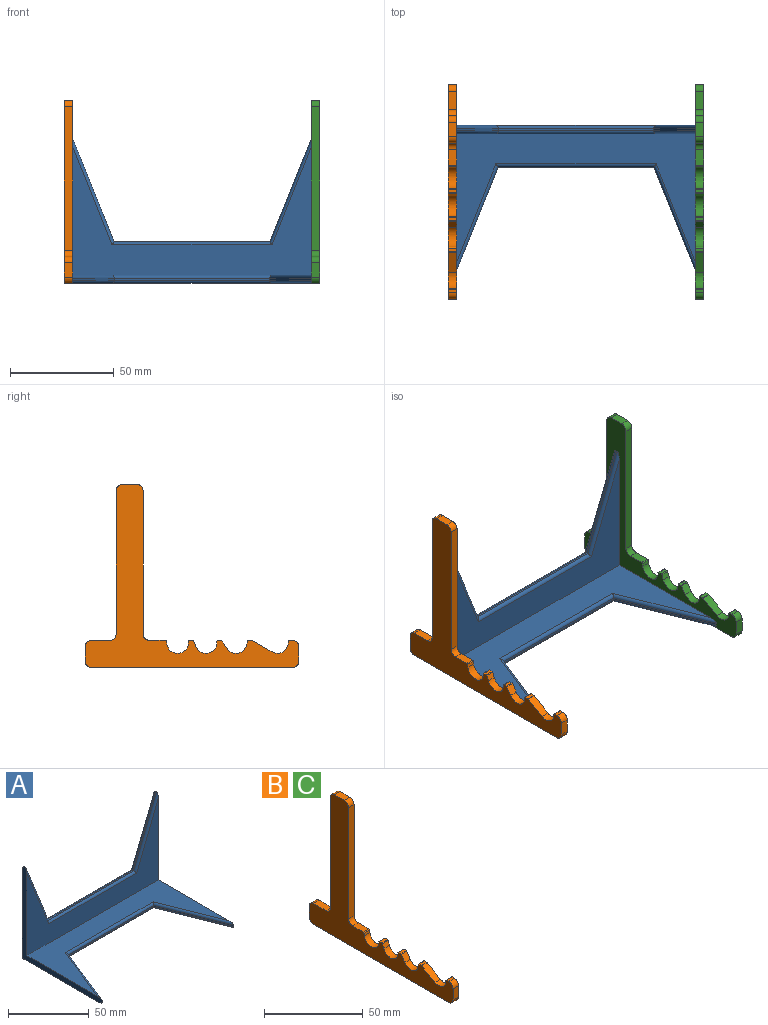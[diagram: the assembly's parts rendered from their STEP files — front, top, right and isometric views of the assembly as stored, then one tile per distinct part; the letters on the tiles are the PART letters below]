
ASSEMBLY  parts=3 mates=2
PART A: 25 faces, bbox 117.8x70x70 mm
  f0: plane 115x61.96mm, normal (0,-1,0), area 2568.5mm2, adj f5,f6,f7,f15,f16,f17
  f1: plane 115x64.46mm, normal (0,1,0), area 2856mm2, adj f6,f7,f12,f13,f14,f24
  f2: plane 75x1mm, normal (0,0,1), area 75mm2, adj f10,f11,f13,f16
  f3: plane 75x1mm, normal (0,-1,0), area 75mm2, adj f8,f9,f19,f22
  f4: plane 115x64.46mm, normal (0,0,-1), area 2856mm2, adj f6,f7,f18,f19,f20,f24
  f5: plane 115x61.96mm, normal (0,0,1), area 2568.5mm2, adj f0,f6,f7,f21,f22,f23
  f6: plane 70x70mm, normal (1,0,0), area 538.3mm2, adj f0,f1,f4,f5,f9,f10,f12,f17
  f7: plane 70x70mm, normal (-1,0,0), area 538.3mm2, adj f0,f1,f4,f5,f8,f11,f14,f15
  f8: plane 50x20mm, normal (0.93,-0.37,0), area 53.9mm2, adj f3,f7,f18,f23
  f9: plane 50x20mm, normal (-0.93,-0.37,0), area 53.9mm2, adj f3,f6,f20,f21
  f10: plane 50x20mm, normal (-0.93,0,0.37), area 53.9mm2, adj f2,f6,f12,f17
  f11: plane 50x20mm, normal (0.93,0,0.37), area 53.9mm2, adj f2,f7,f14,f15
  f12: cylinder r=1.5mm len=51.5mm, axis (0.37,0,0.93), area 124.5mm2, adj f1,f6,f10,f13
  f13: cylinder r=1.5mm len=77.03mm, axis (-1,0,0), area 178.5mm2, adj f1,f2,f12,f14
  f14: cylinder r=1.5mm len=51.5mm, axis (0.37,0,-0.93), area 124.5mm2, adj f1,f7,f11,f13
  f15: cylinder r=1.5mm len=51.5mm, axis (-0.37,0,0.93), area 124.5mm2, adj f0,f7,f11,f16
  f16: cylinder r=1.5mm len=77.03mm, axis (-1,0,0), area 178.5mm2, adj f0,f2,f15,f17
  f17: cylinder r=1.5mm len=51.5mm, axis (-0.37,0,-0.93), area 124.5mm2, adj f0,f6,f10,f16
  f18: cylinder r=1.5mm len=51.5mm, axis (-0.37,-0.93,0), area 124.5mm2, adj f4,f7,f8,f19
  f19: cylinder r=1.5mm len=77.03mm, axis (-1,0,0), area 178.5mm2, adj f3,f4,f18,f20
  f20: cylinder r=1.5mm len=51.5mm, axis (-0.37,0.93,0), area 124.5mm2, adj f4,f6,f9,f19
  f21: cylinder r=1.5mm len=51.5mm, axis (0.37,-0.93,0), area 124.5mm2, adj f5,f6,f9,f22
  f22: cylinder r=1.5mm len=77.03mm, axis (-1,0,0), area 178.5mm2, adj f3,f5,f21,f23
  f23: cylinder r=1.5mm len=51.5mm, axis (0.37,0.93,0), area 124.5mm2, adj f5,f7,f8,f22
  f24: cylinder r=1.5mm len=115mm, axis (-1,0,0), area 271mm2, adj f1,f4,f6,f7
PART B: 38 faces, bbox 4x103x88 mm
  f0: plane 4x1.6mm, normal (0,0,1), area 6.4mm2, adj f1,f3,f31,f32
  f1: plane 103x88mm, normal (1,0,0), area 2071.5mm2, adj f0,f2,f4,f5,f6,f7,f8,f9
  f2: plane 4x1.48mm, normal (0,0,1), area 5.9mm2, adj f1,f3,f33,f34
  f3: plane 103x88mm, normal (-1,0,0), area 2071.5mm2, adj f0,f2,f4,f5,f6,f7,f8,f9
  f4: plane 4x1.72mm, normal (0,0,1), area 6.9mm2, adj f1,f3,f35,f36
  f5: plane 4x1.63mm, normal (0,0,1), area 6.5mm2, adj f1,f3,f23,f37
  f6: plane 69x4mm, normal (0,-1,0), area 276mm2, adj f1,f3,f22,f29
  f7: plane 7.67x4mm, normal (0,0,1), area 30.7mm2, adj f1,f3,f22,f30
  f8: plane 7x4mm, normal (0,-1,0), area 28mm2, adj f1,f3,f23,f24
  f9: plane 97x4mm, normal (0,0,-1), area 388mm2, adj f1,f3,f24,f25
  f10: plane 7x4mm, normal (0,1,0), area 28mm2, adj f1,f3,f25,f26
  f11: plane 9x4mm, normal (0,0,1), area 36mm2, adj f1,f3,f26,f27
  f12: plane 69x4mm, normal (0,1,0), area 276mm2, adj f1,f3,f27,f28
  f13: plane 7x4mm, normal (0,0,1), area 28mm2, adj f1,f3,f28,f29
  f14: cylinder r=5.25mm len=7.86mm, axis (1,0,0), area 45.7mm2, adj f1,f3,f15,f37
  f15: plane 9.58x5.49mm, normal (0,-0.5,0.87), area 44.2mm2, adj f1,f3,f14,f36
  f16: plane 4x3.75mm, normal (0,-0.82,0.57), area 18.2mm2, adj f1,f3,f17,f34
  f17: cylinder r=5.25mm len=9.58mm, axis (1,0,0), area 55.2mm2, adj f1,f3,f16,f35
  f18: plane 4x2.54mm, normal (0,-0.94,0.35), area 10.9mm2, adj f1,f3,f19,f32
  f19: cylinder r=5.25mm len=10.16mm, axis (1,0,0), area 60.2mm2, adj f1,f3,f18,f33
  f20: plane 4x1.42mm, normal (0,-0.99,0.16), area 5.7mm2, adj f1,f3,f21,f30
  f21: cylinder r=5.25mm len=10.43mm, axis (1,0,0), area 64.4mm2, adj f1,f3,f20,f31
  f22: cylinder r=3mm len=4mm, axis (-1,0,0), area 18.8mm2, adj f1,f3,f6,f7
  f23: cylinder r=3mm len=4mm, axis (-1,0,0), area 18.8mm2, adj f1,f3,f5,f8
  f24: cylinder r=3mm len=4mm, axis (-1,0,0), area 18.8mm2, adj f1,f3,f8,f9
  f25: cylinder r=3mm len=4mm, axis (-1,0,0), area 18.8mm2, adj f1,f3,f9,f10
  f26: cylinder r=3mm len=4mm, axis (1,0,0), area 18.8mm2, adj f1,f3,f10,f11
  f27: cylinder r=3mm len=4mm, axis (1,0,0), area 18.8mm2, adj f1,f3,f11,f12
  f28: cylinder r=3mm len=4mm, axis (-1,0,0), area 18.8mm2, adj f1,f3,f12,f13
  f29: cylinder r=3mm len=4mm, axis (-1,0,0), area 18.8mm2, adj f1,f3,f6,f13
  f30: cylinder r=0.5mm len=4mm, axis (1,0,0), area 2.8mm2, adj f1,f3,f7,f20
  f31: cylinder r=0.5mm len=4mm, axis (1,0,0), area 3.3mm2, adj f0,f1,f3,f21
  f32: cylinder r=0.5mm len=4mm, axis (1,0,0), area 2.4mm2, adj f0,f1,f3,f18
  f33: cylinder r=0.5mm len=4mm, axis (1,0,0), area 3.3mm2, adj f1,f2,f3,f19
  f34: cylinder r=0.5mm len=4mm, axis (1,0,0), area 1.9mm2, adj f1,f2,f3,f16
  f35: cylinder r=0.5mm len=4mm, axis (1,0,0), area 3.3mm2, adj f1,f3,f4,f17
  f36: cylinder r=0.5mm len=4mm, axis (1,0,0), area 1mm2, adj f1,f3,f4,f15
  f37: cylinder r=0.5mm len=4mm, axis (1,0,0), area 3.3mm2, adj f1,f3,f5,f14
PART C: same geometry as B
PLACE A t=(-148.98,48.79,-23.77)mm
PLACE B t=(-152.98,40.29,-10.77)mm
PLACE C t=(-33.98,40.29,-10.77)mm fixed
MATE fastened B.f26 <-> C.f26  axis (1,0,0) through (-148.98,65.29,-13.77)mm
MATE fastened A.f7 <-> B.f1  axis (-1,0,0) through (-148.98,46.79,46.23)mm
